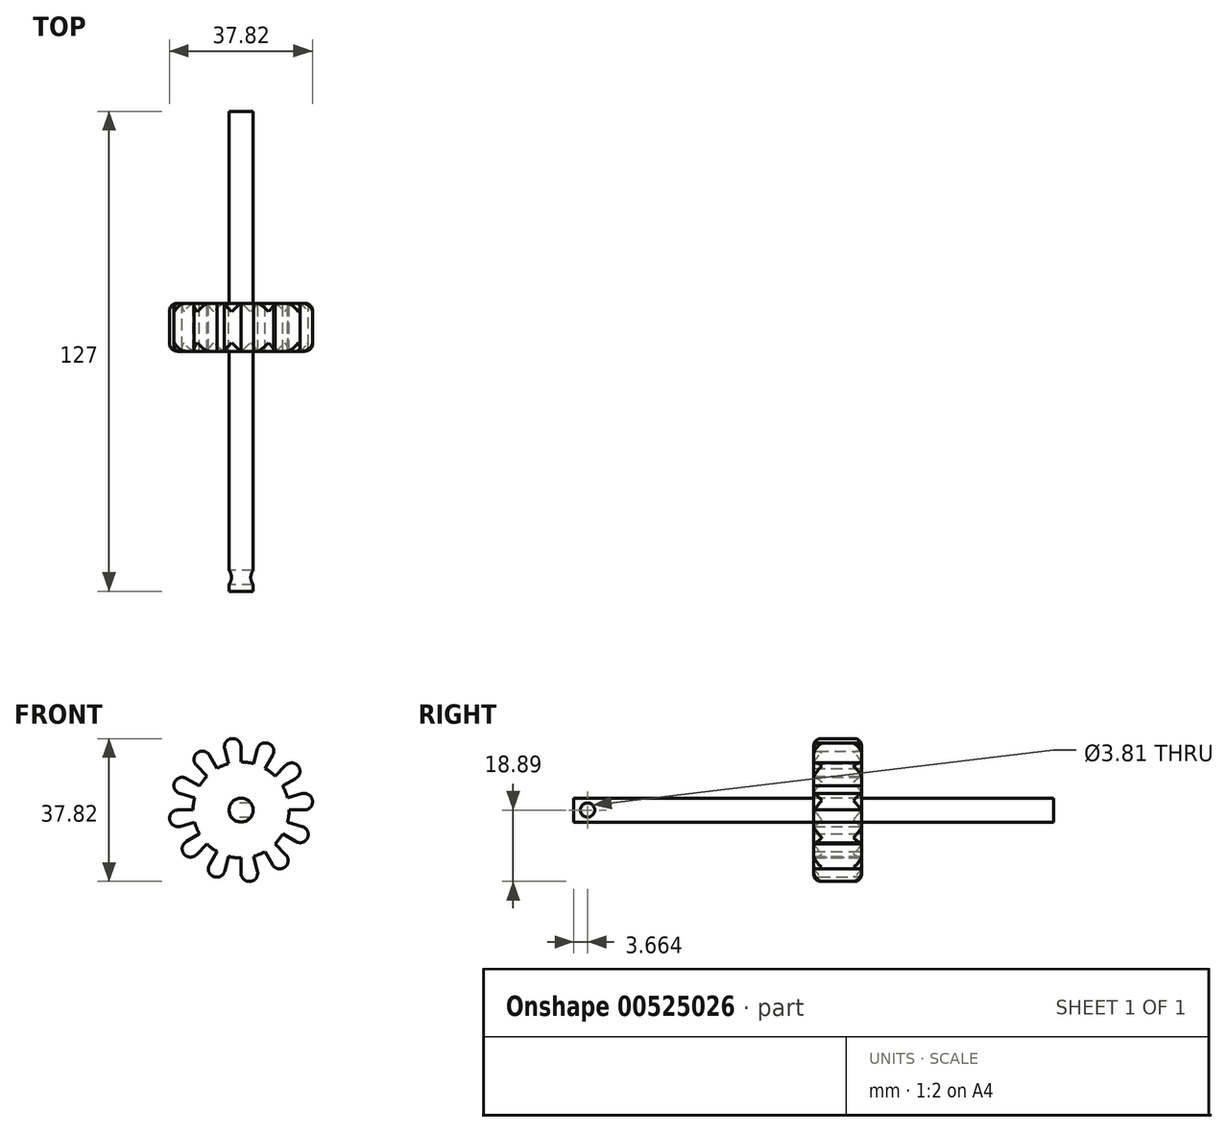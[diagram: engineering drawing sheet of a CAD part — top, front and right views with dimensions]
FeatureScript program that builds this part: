
annotation { "Feature Type Name" : "Feature", "Feature Type Description" : "" }
export const myFeature = defineFeature(function(context is Context, id is Id, definition is map)
    precondition{}
    {
        {
            var Q0;
            Q0=qCreatedBy(makeId("Front.planeOp"),FACE);
            var sketch = newSketch(context, id + "F0", { "sketchPlane" : qUnion([Q0])});
            skCircle(sketch, "E0", {"center": v(-0.02, 0.02) * mm, "radius": 12.7 * mm});
            skCircle(sketch, "E1", {"center": v(-0.02, 0.02) * mm, "radius": 19.05 * mm});
            skLineSegment(sketch, "E2", {"start": v(-0.02, 0.02) * mm, "end": v(-0.02, 19.07) * mm});
            skLineSegment(sketch, "E3", {"start": v(-0.02, 0.02) * mm, "end": v(4.91, 18.42) * mm});
            skLineSegment(sketch, "E4", {"start": v(-0.02, 0.02) * mm, "end": v(9.5, 16.52) * mm});
            skLineSegment(sketch, "E5", {"start": v(-0.02, 0.02) * mm, "end": v(13.45, 13.5) * mm});
            skLineSegment(sketch, "E6", {"start": v(-0.02, 0.02) * mm, "end": v(16.48, 9.55) * mm});
            skLineSegment(sketch, "E7", {"start": v(-0.02, 0.02) * mm, "end": v(18.38, 4.95) * mm});
            skLineSegment(sketch, "E8", {"start": v(-0.02, 0.02) * mm, "end": v(19.03, 0.02) * mm});
            skLineSegment(sketch, "E9", {"start": v(-0.02, 0.02) * mm, "end": v(18.38, -4.9) * mm});
            skLineSegment(sketch, "E10", {"start": v(-0.02, 0.02) * mm, "end": v(16.48, -9.5) * mm});
            skLineSegment(sketch, "E11", {"start": v(-0.02, 0.02) * mm, "end": v(13.45, -13.45) * mm});
            skLineSegment(sketch, "E12", {"start": v(-0.02, 0.02) * mm, "end": v(9.5, -16.48) * mm});
            skLineSegment(sketch, "E13", {"start": v(-0.02, 0.02) * mm, "end": v(4.91, -18.38) * mm});
            skLineSegment(sketch, "E14", {"start": v(-0.02, 0.02) * mm, "end": v(-0.02, -19.03) * mm});
            skLineSegment(sketch, "E15", {"start": v(-0.02, 0.02) * mm, "end": v(-4.95, -18.38) * mm});
            skLineSegment(sketch, "E16", {"start": v(-0.02, 0.02) * mm, "end": v(-9.54, -16.48) * mm});
            skLineSegment(sketch, "E17", {"start": v(-0.02, 0.02) * mm, "end": v(-13.49, -13.45) * mm});
            skLineSegment(sketch, "E18", {"start": v(-0.02, 0.02) * mm, "end": v(-16.51, -9.5) * mm});
            skLineSegment(sketch, "E19", {"start": v(-0.02, 0.02) * mm, "end": v(-18.42, -4.9) * mm});
            skLineSegment(sketch, "E20", {"start": v(-0.02, 0.02) * mm, "end": v(-19.07, 0.02) * mm});
            skLineSegment(sketch, "E21", {"start": v(-0.02, 0.02) * mm, "end": v(-13.49, 13.5) * mm});
            skLineSegment(sketch, "E22", {"start": v(-0.02, 0.02) * mm, "end": v(-16.51, 9.55) * mm});
            skLineSegment(sketch, "E23", {"start": v(-0.02, 0.02) * mm, "end": v(-18.42, 4.95) * mm});
            skLineSegment(sketch, "E24", {"start": v(-0.02, 0.02) * mm, "end": v(-4.95, 18.42) * mm});
            skLineSegment(sketch, "E25", {"start": v(-0.02, 0.02) * mm, "end": v(-9.54, 16.52) * mm});
            skSolve(sketch);
        }
        {
            var Q0;
            {var subQ0=sQuery(id+"F0.wireOp",EDGE,"E13");var subQ1=sQuery(id+"F0.wireOp",EDGE,"E0");var subQ2=makeQuery(id+"F0.imprint","INTERSECT",VERTEX,{"derivedFrom":[subQ1,subQ0]});Q0=makeQuery(id+"F0.imprint","IMPRINT",FACE,{"disambiguationData":[TD([[makeQuery(id+"F0.imprint","IMPRINT",EDGE,{"disambiguationData":[TD([[subQ2,-1.0]])],"derivedFrom":subQ1}),1.0]])]});}
            var Q1;
            {var subQ0=sQuery(id+"F0.wireOp",EDGE,"E15");var subQ1=sQuery(id+"F0.wireOp",EDGE,"E0");var subQ2=makeQuery(id+"F0.imprint","INTERSECT",VERTEX,{"derivedFrom":[subQ1,subQ0]});Q1=makeQuery(id+"F0.imprint","IMPRINT",FACE,{"disambiguationData":[TD([[makeQuery(id+"F0.imprint","IMPRINT",EDGE,{"disambiguationData":[TD([[subQ2,-1.0]])],"derivedFrom":subQ1}),1.0]])]});}
            var Q2;
            {var subQ0=sQuery(id+"F0.wireOp",EDGE,"E17");var subQ1=sQuery(id+"F0.wireOp",EDGE,"E0");var subQ2=makeQuery(id+"F0.imprint","INTERSECT",VERTEX,{"derivedFrom":[subQ1,subQ0]});Q2=makeQuery(id+"F0.imprint","IMPRINT",FACE,{"disambiguationData":[TD([[makeQuery(id+"F0.imprint","IMPRINT",EDGE,{"disambiguationData":[TD([[subQ2,-1.0]])],"derivedFrom":subQ1}),1.0]])]});}
            var Q3;
            {var subQ0=sQuery(id+"F0.wireOp",EDGE,"E19");var subQ1=sQuery(id+"F0.wireOp",EDGE,"E0");var subQ2=makeQuery(id+"F0.imprint","INTERSECT",VERTEX,{"derivedFrom":[subQ1,subQ0]});Q3=makeQuery(id+"F0.imprint","IMPRINT",FACE,{"disambiguationData":[TD([[makeQuery(id+"F0.imprint","IMPRINT",EDGE,{"disambiguationData":[TD([[subQ2,-1.0]])],"derivedFrom":subQ1}),1.0]])]});}
            var Q4;
            {var subQ0=sQuery(id+"F0.wireOp",EDGE,"E18");var subQ1=sQuery(id+"F0.wireOp",EDGE,"E0");var subQ2=makeQuery(id+"F0.imprint","INTERSECT",VERTEX,{"derivedFrom":[subQ1,subQ0]});Q4=makeQuery(id+"F0.imprint","IMPRINT",FACE,{"disambiguationData":[TD([[makeQuery(id+"F0.imprint","IMPRINT",EDGE,{"disambiguationData":[TD([[subQ2,-1.0]])],"derivedFrom":subQ1}),1.0]])]});}
            var Q5;
            {var subQ0=sQuery(id+"F0.wireOp",EDGE,"E16");var subQ1=sQuery(id+"F0.wireOp",EDGE,"E0");var subQ2=makeQuery(id+"F0.imprint","INTERSECT",VERTEX,{"derivedFrom":[subQ1,subQ0]});Q5=makeQuery(id+"F0.imprint","IMPRINT",FACE,{"disambiguationData":[TD([[makeQuery(id+"F0.imprint","IMPRINT",EDGE,{"disambiguationData":[TD([[subQ2,-1.0]])],"derivedFrom":subQ1}),1.0]])]});}
            var Q6;
            {var subQ0=sQuery(id+"F0.wireOp",EDGE,"E14");var subQ1=sQuery(id+"F0.wireOp",EDGE,"E0");var subQ2=makeQuery(id+"F0.imprint","INTERSECT",VERTEX,{"derivedFrom":[subQ1,subQ0]});Q6=makeQuery(id+"F0.imprint","IMPRINT",FACE,{"disambiguationData":[TD([[makeQuery(id+"F0.imprint","IMPRINT",EDGE,{"disambiguationData":[TD([[subQ2,-1.0]])],"derivedFrom":subQ1}),1.0]])]});}
            var Q7;
            {var subQ0=sQuery(id+"F0.wireOp",EDGE,"E12");var subQ1=sQuery(id+"F0.wireOp",EDGE,"E0");var subQ2=makeQuery(id+"F0.imprint","INTERSECT",VERTEX,{"derivedFrom":[subQ1,subQ0]});Q7=makeQuery(id+"F0.imprint","IMPRINT",FACE,{"disambiguationData":[TD([[makeQuery(id+"F0.imprint","IMPRINT",EDGE,{"disambiguationData":[TD([[subQ2,-1.0]])],"derivedFrom":subQ1}),1.0]])]});}
            var Q8;
            {var subQ0=sQuery(id+"F0.wireOp",EDGE,"E11");var subQ1=sQuery(id+"F0.wireOp",EDGE,"E0");var subQ2=makeQuery(id+"F0.imprint","INTERSECT",VERTEX,{"derivedFrom":[subQ1,subQ0]});Q8=makeQuery(id+"F0.imprint","IMPRINT",FACE,{"disambiguationData":[TD([[makeQuery(id+"F0.imprint","IMPRINT",EDGE,{"disambiguationData":[TD([[subQ2,-1.0]])],"derivedFrom":subQ1}),1.0]])]});}
            var Q9;
            {var subQ0=sQuery(id+"F0.wireOp",EDGE,"E10");var subQ1=sQuery(id+"F0.wireOp",EDGE,"E0");var subQ2=makeQuery(id+"F0.imprint","INTERSECT",VERTEX,{"derivedFrom":[subQ1,subQ0]});Q9=makeQuery(id+"F0.imprint","IMPRINT",FACE,{"disambiguationData":[TD([[makeQuery(id+"F0.imprint","IMPRINT",EDGE,{"disambiguationData":[TD([[subQ2,-1.0]])],"derivedFrom":subQ1}),1.0]])]});}
            var Q10;
            {var subQ0=sQuery(id+"F0.wireOp",EDGE,"E8");var subQ1=sQuery(id+"F0.wireOp",EDGE,"E0");var subQ2=makeQuery(id+"F0.imprint","INTERSECT",VERTEX,{"derivedFrom":[subQ1,subQ0]});Q10=makeQuery(id+"F0.imprint","IMPRINT",FACE,{"disambiguationData":[TD([[makeQuery(id+"F0.imprint","IMPRINT",EDGE,{"disambiguationData":[TD([[subQ2,1.0]])],"derivedFrom":subQ1}),1.0]])]});}
            var Q11;
            {var subQ0=sQuery(id+"F0.wireOp",EDGE,"E7");var subQ1=sQuery(id+"F0.wireOp",EDGE,"E0");var subQ2=makeQuery(id+"F0.imprint","INTERSECT",VERTEX,{"derivedFrom":[subQ1,subQ0]});Q11=makeQuery(id+"F0.imprint","IMPRINT",FACE,{"disambiguationData":[TD([[makeQuery(id+"F0.imprint","IMPRINT",EDGE,{"disambiguationData":[TD([[subQ2,1.0]])],"derivedFrom":subQ1}),1.0]])]});}
            var Q12;
            {var subQ0=sQuery(id+"F0.wireOp",EDGE,"E7");var subQ1=sQuery(id+"F0.wireOp",EDGE,"E0");var subQ2=makeQuery(id+"F0.imprint","INTERSECT",VERTEX,{"derivedFrom":[subQ1,subQ0]});Q12=makeQuery(id+"F0.imprint","IMPRINT",FACE,{"disambiguationData":[TD([[makeQuery(id+"F0.imprint","IMPRINT",EDGE,{"disambiguationData":[TD([[subQ2,-1.0]])],"derivedFrom":subQ1}),1.0]])]});}
            var Q13;
            {var subQ0=sQuery(id+"F0.wireOp",EDGE,"E6");var subQ1=sQuery(id+"F0.wireOp",EDGE,"E0");var subQ2=makeQuery(id+"F0.imprint","INTERSECT",VERTEX,{"derivedFrom":[subQ1,subQ0]});Q13=makeQuery(id+"F0.imprint","IMPRINT",FACE,{"disambiguationData":[TD([[makeQuery(id+"F0.imprint","IMPRINT",EDGE,{"disambiguationData":[TD([[subQ2,-1.0]])],"derivedFrom":subQ1}),1.0]])]});}
            var Q14;
            {var subQ0=sQuery(id+"F0.wireOp",EDGE,"E5");var subQ1=sQuery(id+"F0.wireOp",EDGE,"E0");var subQ2=makeQuery(id+"F0.imprint","INTERSECT",VERTEX,{"derivedFrom":[subQ1,subQ0]});Q14=makeQuery(id+"F0.imprint","IMPRINT",FACE,{"disambiguationData":[TD([[makeQuery(id+"F0.imprint","IMPRINT",EDGE,{"disambiguationData":[TD([[subQ2,-1.0]])],"derivedFrom":subQ1}),1.0]])]});}
            var Q15;
            {var subQ0=sQuery(id+"F0.wireOp",EDGE,"E4");var subQ1=sQuery(id+"F0.wireOp",EDGE,"E0");var subQ2=makeQuery(id+"F0.imprint","INTERSECT",VERTEX,{"derivedFrom":[subQ1,subQ0]});Q15=makeQuery(id+"F0.imprint","IMPRINT",FACE,{"disambiguationData":[TD([[makeQuery(id+"F0.imprint","IMPRINT",EDGE,{"disambiguationData":[TD([[subQ2,-1.0]])],"derivedFrom":subQ1}),1.0]])]});}
            var Q16;
            {var subQ0=sQuery(id+"F0.wireOp",EDGE,"E3");var subQ1=sQuery(id+"F0.wireOp",EDGE,"E0");var subQ2=makeQuery(id+"F0.imprint","INTERSECT",VERTEX,{"derivedFrom":[subQ1,subQ0]});Q16=makeQuery(id+"F0.imprint","IMPRINT",FACE,{"disambiguationData":[TD([[makeQuery(id+"F0.imprint","IMPRINT",EDGE,{"disambiguationData":[TD([[subQ2,-1.0]])],"derivedFrom":subQ1}),1.0]])]});}
            var Q17;
            {var subQ0=sQuery(id+"F0.wireOp",EDGE,"E2");var subQ1=sQuery(id+"F0.wireOp",EDGE,"E0");var subQ2=makeQuery(id+"F0.imprint","INTERSECT",VERTEX,{"derivedFrom":[subQ1,subQ0]});Q17=makeQuery(id+"F0.imprint","IMPRINT",FACE,{"disambiguationData":[TD([[makeQuery(id+"F0.imprint","IMPRINT",EDGE,{"disambiguationData":[TD([[subQ2,-1.0]])],"derivedFrom":subQ1}),1.0]])]});}
            var Q18;
            {var subQ0=sQuery(id+"F0.wireOp",EDGE,"E24");var subQ1=sQuery(id+"F0.wireOp",EDGE,"E0");var subQ2=makeQuery(id+"F0.imprint","INTERSECT",VERTEX,{"derivedFrom":[subQ1,subQ0]});Q18=makeQuery(id+"F0.imprint","IMPRINT",FACE,{"disambiguationData":[TD([[makeQuery(id+"F0.imprint","IMPRINT",EDGE,{"disambiguationData":[TD([[subQ2,-1.0]])],"derivedFrom":subQ1}),1.0]])]});}
            var Q19;
            {var subQ0=sQuery(id+"F0.wireOp",EDGE,"E25");var subQ1=sQuery(id+"F0.wireOp",EDGE,"E0");var subQ2=makeQuery(id+"F0.imprint","INTERSECT",VERTEX,{"derivedFrom":[subQ1,subQ0]});Q19=makeQuery(id+"F0.imprint","IMPRINT",FACE,{"disambiguationData":[TD([[makeQuery(id+"F0.imprint","IMPRINT",EDGE,{"disambiguationData":[TD([[subQ2,-1.0]])],"derivedFrom":subQ1}),1.0]])]});}
            var Q20;
            {var subQ0=sQuery(id+"F0.wireOp",EDGE,"E21");var subQ1=sQuery(id+"F0.wireOp",EDGE,"E0");var subQ2=makeQuery(id+"F0.imprint","INTERSECT",VERTEX,{"derivedFrom":[subQ1,subQ0]});Q20=makeQuery(id+"F0.imprint","IMPRINT",FACE,{"disambiguationData":[TD([[makeQuery(id+"F0.imprint","IMPRINT",EDGE,{"disambiguationData":[TD([[subQ2,-1.0]])],"derivedFrom":subQ1}),1.0]])]});}
            var Q21;
            {var subQ0=sQuery(id+"F0.wireOp",EDGE,"E22");var subQ1=sQuery(id+"F0.wireOp",EDGE,"E0");var subQ2=makeQuery(id+"F0.imprint","INTERSECT",VERTEX,{"derivedFrom":[subQ1,subQ0]});Q21=makeQuery(id+"F0.imprint","IMPRINT",FACE,{"disambiguationData":[TD([[makeQuery(id+"F0.imprint","IMPRINT",EDGE,{"disambiguationData":[TD([[subQ2,-1.0]])],"derivedFrom":subQ1}),1.0]])]});}
            var Q22;
            {var subQ0=sQuery(id+"F0.wireOp",EDGE,"E23");var subQ1=sQuery(id+"F0.wireOp",EDGE,"E0");var subQ2=makeQuery(id+"F0.imprint","INTERSECT",VERTEX,{"derivedFrom":[subQ1,subQ0]});Q22=makeQuery(id+"F0.imprint","IMPRINT",FACE,{"disambiguationData":[TD([[makeQuery(id+"F0.imprint","IMPRINT",EDGE,{"disambiguationData":[TD([[subQ2,-1.0]])],"derivedFrom":subQ1}),1.0]])]});}
            var Q23;
            {var subQ0=sQuery(id+"F0.wireOp",EDGE,"E20");var subQ1=sQuery(id+"F0.wireOp",EDGE,"E0");var subQ2=makeQuery(id+"F0.imprint","INTERSECT",VERTEX,{"derivedFrom":[subQ1,subQ0]});Q23=makeQuery(id+"F0.imprint","IMPRINT",FACE,{"disambiguationData":[TD([[makeQuery(id+"F0.imprint","IMPRINT",EDGE,{"disambiguationData":[TD([[subQ2,-1.0]])],"derivedFrom":subQ1}),1.0]])]});}
            var Q24;
            {var subQ0=sQuery(id+"F0.wireOp",EDGE,"E22");var subQ1=sQuery(id+"F0.wireOp",EDGE,"E0");var subQ2=makeQuery(id+"F0.imprint","INTERSECT",VERTEX,{"derivedFrom":[subQ1,subQ0]});Q24=makeQuery(id+"F0.imprint","IMPRINT",FACE,{"disambiguationData":[TD([[makeQuery(id+"F0.imprint","IMPRINT",EDGE,{"disambiguationData":[TD([[subQ2,-1.0]])],"derivedFrom":subQ1}),-1.0]])]});}
            var Q25;
            {var subQ0=sQuery(id+"F0.wireOp",EDGE,"E20");var subQ1=sQuery(id+"F0.wireOp",EDGE,"E0");var subQ2=makeQuery(id+"F0.imprint","INTERSECT",VERTEX,{"derivedFrom":[subQ1,subQ0]});Q25=makeQuery(id+"F0.imprint","IMPRINT",FACE,{"disambiguationData":[TD([[makeQuery(id+"F0.imprint","IMPRINT",EDGE,{"disambiguationData":[TD([[subQ2,-1.0]])],"derivedFrom":subQ1}),-1.0]])]});}
            var Q26;
            {var subQ0=sQuery(id+"F0.wireOp",EDGE,"E18");var subQ1=sQuery(id+"F0.wireOp",EDGE,"E0");var subQ2=makeQuery(id+"F0.imprint","INTERSECT",VERTEX,{"derivedFrom":[subQ1,subQ0]});Q26=makeQuery(id+"F0.imprint","IMPRINT",FACE,{"disambiguationData":[TD([[makeQuery(id+"F0.imprint","IMPRINT",EDGE,{"disambiguationData":[TD([[subQ2,-1.0]])],"derivedFrom":subQ1}),-1.0]])]});}
            var Q27;
            {var subQ0=sQuery(id+"F0.wireOp",EDGE,"E16");var subQ1=sQuery(id+"F0.wireOp",EDGE,"E0");var subQ2=makeQuery(id+"F0.imprint","INTERSECT",VERTEX,{"derivedFrom":[subQ1,subQ0]});Q27=makeQuery(id+"F0.imprint","IMPRINT",FACE,{"disambiguationData":[TD([[makeQuery(id+"F0.imprint","IMPRINT",EDGE,{"disambiguationData":[TD([[subQ2,-1.0]])],"derivedFrom":subQ1}),-1.0]])]});}
            var Q28;
            {var subQ0=sQuery(id+"F0.wireOp",EDGE,"E10");var subQ1=sQuery(id+"F0.wireOp",EDGE,"E0");var subQ2=makeQuery(id+"F0.imprint","INTERSECT",VERTEX,{"derivedFrom":[subQ1,subQ0]});Q28=makeQuery(id+"F0.imprint","IMPRINT",FACE,{"disambiguationData":[TD([[makeQuery(id+"F0.imprint","IMPRINT",EDGE,{"disambiguationData":[TD([[subQ2,-1.0]])],"derivedFrom":subQ1}),-1.0]])]});}
            var Q29;
            {var subQ0=sQuery(id+"F0.wireOp",EDGE,"E7");var subQ1=sQuery(id+"F0.wireOp",EDGE,"E0");var subQ2=makeQuery(id+"F0.imprint","INTERSECT",VERTEX,{"derivedFrom":[subQ1,subQ0]});Q29=makeQuery(id+"F0.imprint","IMPRINT",FACE,{"disambiguationData":[TD([[makeQuery(id+"F0.imprint","IMPRINT",EDGE,{"disambiguationData":[TD([[subQ2,1.0]])],"derivedFrom":subQ1}),-1.0]])]});}
            var Q30;
            {var subQ0=sQuery(id+"F0.wireOp",EDGE,"E6");var subQ1=sQuery(id+"F0.wireOp",EDGE,"E0");var subQ2=makeQuery(id+"F0.imprint","INTERSECT",VERTEX,{"derivedFrom":[subQ1,subQ0]});Q30=makeQuery(id+"F0.imprint","IMPRINT",FACE,{"disambiguationData":[TD([[makeQuery(id+"F0.imprint","IMPRINT",EDGE,{"disambiguationData":[TD([[subQ2,-1.0]])],"derivedFrom":subQ1}),-1.0]])]});}
            var Q31;
            {var subQ0=sQuery(id+"F0.wireOp",EDGE,"E4");var subQ1=sQuery(id+"F0.wireOp",EDGE,"E0");var subQ2=makeQuery(id+"F0.imprint","INTERSECT",VERTEX,{"derivedFrom":[subQ1,subQ0]});Q31=makeQuery(id+"F0.imprint","IMPRINT",FACE,{"disambiguationData":[TD([[makeQuery(id+"F0.imprint","IMPRINT",EDGE,{"disambiguationData":[TD([[subQ2,-1.0]])],"derivedFrom":subQ1}),-1.0]])]});}
            var Q32;
            {var subQ0=sQuery(id+"F0.wireOp",EDGE,"E2");var subQ1=sQuery(id+"F0.wireOp",EDGE,"E0");var subQ2=makeQuery(id+"F0.imprint","INTERSECT",VERTEX,{"derivedFrom":[subQ1,subQ0]});Q32=makeQuery(id+"F0.imprint","IMPRINT",FACE,{"disambiguationData":[TD([[makeQuery(id+"F0.imprint","IMPRINT",EDGE,{"disambiguationData":[TD([[subQ2,-1.0]])],"derivedFrom":subQ1}),-1.0]])]});}
            var Q33;
            {var subQ0=sQuery(id+"F0.wireOp",EDGE,"E25");var subQ1=sQuery(id+"F0.wireOp",EDGE,"E0");var subQ2=makeQuery(id+"F0.imprint","INTERSECT",VERTEX,{"derivedFrom":[subQ1,subQ0]});Q33=makeQuery(id+"F0.imprint","IMPRINT",FACE,{"disambiguationData":[TD([[makeQuery(id+"F0.imprint","IMPRINT",EDGE,{"disambiguationData":[TD([[subQ2,-1.0]])],"derivedFrom":subQ1}),-1.0]])]});}
            var Q34;
            {var subQ0=sQuery(id+"F0.wireOp",EDGE,"E14");var subQ1=sQuery(id+"F0.wireOp",EDGE,"E0");var subQ2=makeQuery(id+"F0.imprint","INTERSECT",VERTEX,{"derivedFrom":[subQ1,subQ0]});Q34=makeQuery(id+"F0.imprint","IMPRINT",FACE,{"disambiguationData":[TD([[makeQuery(id+"F0.imprint","IMPRINT",EDGE,{"disambiguationData":[TD([[subQ2,-1.0]])],"derivedFrom":subQ1}),-1.0]])]});}
            var Q35;
            {var subQ0=sQuery(id+"F0.wireOp",EDGE,"E12");var subQ1=sQuery(id+"F0.wireOp",EDGE,"E0");var subQ2=makeQuery(id+"F0.imprint","INTERSECT",VERTEX,{"derivedFrom":[subQ1,subQ0]});Q35=makeQuery(id+"F0.imprint","IMPRINT",FACE,{"disambiguationData":[TD([[makeQuery(id+"F0.imprint","IMPRINT",EDGE,{"disambiguationData":[TD([[subQ2,-1.0]])],"derivedFrom":subQ1}),-1.0]])]});}
            extrude(context, id + "F1", {"entities" : qUnion([Q0, Q1, Q2, Q3, Q4, Q5, Q6, Q7, Q8, Q9, Q10, Q11, Q12, Q13, Q14, Q15, Q16, Q17, Q18, Q19, Q20, Q21, Q22, Q23, Q24, Q25, Q26, Q27, Q28, Q29, Q30, Q31, Q32, Q33, Q34, Q35]), "depth" : 12.7 * mm, "offsetDistance" : 25.4 * mm});
        }
        {
            var Q0;
            {var subQ0=sQuery(id+"F0.wireOp",EDGE,"E1");Q0=makeQuery(id+"F1.opExtrude","SWEPT_FACE",FACE,{"disambiguationData":[OSD([subQ0]),TDD([makeQuery(id+"F0.imprint","IMPRINT",EDGE,{"disambiguationData":[TD([[makeQuery(id+"F0.imprint","INTERSECT",VERTEX,{"derivedFrom":[subQ0,sQuery(id+"F0.wireOp",EDGE,"E11")]}),1.0]])],"derivedFrom":subQ0})])]});}
            var Q1;
            {var subQ0=sQuery(id+"F0.wireOp",EDGE,"E1");Q1=makeQuery(id+"F1.opExtrude","SWEPT_FACE",FACE,{"disambiguationData":[OSD([subQ0]),TDD([makeQuery(id+"F0.imprint","IMPRINT",EDGE,{"disambiguationData":[TD([[makeQuery(id+"F0.imprint","INTERSECT",VERTEX,{"derivedFrom":[subQ0,sQuery(id+"F0.wireOp",EDGE,"E9")]}),1.0]])],"derivedFrom":subQ0})])]});}
            var Q2;
            {var subQ0=sQuery(id+"F0.wireOp",EDGE,"E1");Q2=makeQuery(id+"F1.opExtrude","SWEPT_FACE",FACE,{"disambiguationData":[OSD([subQ0]),TDD([makeQuery(id+"F0.imprint","IMPRINT",EDGE,{"disambiguationData":[TD([[makeQuery(id+"F0.imprint","INTERSECT",VERTEX,{"derivedFrom":[subQ0,sQuery(id+"F0.wireOp",EDGE,"E13")]}),1.0]])],"derivedFrom":subQ0})])]});}
            var Q3;
            {var subQ0=sQuery(id+"F0.wireOp",EDGE,"E1");Q3=makeQuery(id+"F1.opExtrude","SWEPT_FACE",FACE,{"disambiguationData":[OSD([subQ0]),TDD([makeQuery(id+"F0.imprint","IMPRINT",EDGE,{"disambiguationData":[TD([[makeQuery(id+"F0.imprint","INTERSECT",VERTEX,{"derivedFrom":[subQ0,sQuery(id+"F0.wireOp",EDGE,"E7")]}),1.0]])],"derivedFrom":subQ0})])]});}
            var Q4;
            {var subQ0=sQuery(id+"F0.wireOp",EDGE,"E1");Q4=makeQuery(id+"F1.opExtrude","SWEPT_FACE",FACE,{"disambiguationData":[OSD([subQ0]),TDD([makeQuery(id+"F0.imprint","IMPRINT",EDGE,{"disambiguationData":[TD([[makeQuery(id+"F0.imprint","INTERSECT",VERTEX,{"derivedFrom":[subQ0,sQuery(id+"F0.wireOp",EDGE,"E5")]}),1.0]])],"derivedFrom":subQ0})])]});}
            var Q5;
            {var subQ0=sQuery(id+"F0.wireOp",EDGE,"E1");Q5=makeQuery(id+"F1.opExtrude","SWEPT_FACE",FACE,{"disambiguationData":[OSD([subQ0]),TDD([makeQuery(id+"F0.imprint","IMPRINT",EDGE,{"disambiguationData":[TD([[makeQuery(id+"F0.imprint","INTERSECT",VERTEX,{"derivedFrom":[subQ0,sQuery(id+"F0.wireOp",EDGE,"E3")]}),1.0]])],"derivedFrom":subQ0})])]});}
            var Q6;
            {var subQ0=sQuery(id+"F0.wireOp",EDGE,"E1");Q6=makeQuery(id+"F1.opExtrude","SWEPT_FACE",FACE,{"disambiguationData":[OSD([subQ0]),TDD([makeQuery(id+"F0.imprint","IMPRINT",EDGE,{"disambiguationData":[TD([[makeQuery(id+"F0.imprint","INTERSECT",VERTEX,{"derivedFrom":[subQ0,sQuery(id+"F0.wireOp",EDGE,"E2")]}),-1.0]])],"derivedFrom":subQ0})])]});}
            var Q7;
            {var subQ0=sQuery(id+"F0.wireOp",EDGE,"E1");Q7=makeQuery(id+"F1.opExtrude","SWEPT_FACE",FACE,{"disambiguationData":[OSD([subQ0]),TDD([makeQuery(id+"F0.imprint","IMPRINT",EDGE,{"disambiguationData":[TD([[makeQuery(id+"F0.imprint","INTERSECT",VERTEX,{"derivedFrom":[subQ0,sQuery(id+"F0.wireOp",EDGE,"E21")]}),1.0]])],"derivedFrom":subQ0})])]});}
            var Q8;
            {var subQ0=sQuery(id+"F0.wireOp",EDGE,"E1");Q8=makeQuery(id+"F1.opExtrude","SWEPT_FACE",FACE,{"disambiguationData":[OSD([subQ0]),TDD([makeQuery(id+"F0.imprint","IMPRINT",EDGE,{"disambiguationData":[TD([[makeQuery(id+"F0.imprint","INTERSECT",VERTEX,{"derivedFrom":[subQ0,sQuery(id+"F0.wireOp",EDGE,"E22")]}),-1.0]])],"derivedFrom":subQ0})])]});}
            var Q9;
            {var subQ0=sQuery(id+"F0.wireOp",EDGE,"E1");Q9=makeQuery(id+"F1.opExtrude","SWEPT_FACE",FACE,{"disambiguationData":[OSD([subQ0]),TDD([makeQuery(id+"F0.imprint","IMPRINT",EDGE,{"disambiguationData":[TD([[makeQuery(id+"F0.imprint","INTERSECT",VERTEX,{"derivedFrom":[subQ0,sQuery(id+"F0.wireOp",EDGE,"E19")]}),1.0]])],"derivedFrom":subQ0})])]});}
            var Q10;
            {var subQ0=sQuery(id+"F0.wireOp",EDGE,"E1");Q10=makeQuery(id+"F1.opExtrude","SWEPT_FACE",FACE,{"disambiguationData":[OSD([subQ0]),TDD([makeQuery(id+"F0.imprint","IMPRINT",EDGE,{"disambiguationData":[TD([[makeQuery(id+"F0.imprint","INTERSECT",VERTEX,{"derivedFrom":[subQ0,sQuery(id+"F0.wireOp",EDGE,"E17")]}),1.0]])],"derivedFrom":subQ0})])]});}
            var Q11;
            {var subQ0=sQuery(id+"F0.wireOp",EDGE,"E1");Q11=makeQuery(id+"F1.opExtrude","SWEPT_FACE",FACE,{"disambiguationData":[OSD([subQ0]),TDD([makeQuery(id+"F0.imprint","IMPRINT",EDGE,{"disambiguationData":[TD([[makeQuery(id+"F0.imprint","INTERSECT",VERTEX,{"derivedFrom":[subQ0,sQuery(id+"F0.wireOp",EDGE,"E15")]}),1.0]])],"derivedFrom":subQ0})])]});}
            fillet(context, id + "F2", {"entities" : qUnion([Q0, Q1, Q2, Q3, Q4, Q5, Q6, Q7, Q8, Q9, Q10, Q11]), "radius" : 2.18 * mm, "tangentPropagation" : true, "allowEdgeOverflow" : false});
        }
        {
            var Q0;
            Q0=makeQuery(id+"F1.opExtrude","CAP_FACE",FACE,{"disambiguationData":[OSD([sQuery(id+"F0.wireOp",EDGE,"E0"),sQuery(id+"F0.wireOp",EDGE,"E1"),sQuery(id+"F0.wireOp",EDGE,"E2"),sQuery(id+"F0.wireOp",EDGE,"E3"),sQuery(id+"F0.wireOp",EDGE,"E4"),sQuery(id+"F0.wireOp",EDGE,"E5"),sQuery(id+"F0.wireOp",EDGE,"E6"),sQuery(id+"F0.wireOp",EDGE,"E7"),sQuery(id+"F0.wireOp",EDGE,"E8"),sQuery(id+"F0.wireOp",EDGE,"E9"),sQuery(id+"F0.wireOp",EDGE,"E10"),sQuery(id+"F0.wireOp",EDGE,"E11"),sQuery(id+"F0.wireOp",EDGE,"E12"),sQuery(id+"F0.wireOp",EDGE,"E13"),sQuery(id+"F0.wireOp",EDGE,"E14"),sQuery(id+"F0.wireOp",EDGE,"E15"),sQuery(id+"F0.wireOp",EDGE,"E16"),sQuery(id+"F0.wireOp",EDGE,"E17"),sQuery(id+"F0.wireOp",EDGE,"E18"),sQuery(id+"F0.wireOp",EDGE,"E19"),sQuery(id+"F0.wireOp",EDGE,"E20"),sQuery(id+"F0.wireOp",EDGE,"E21"),sQuery(id+"F0.wireOp",EDGE,"E22"),sQuery(id+"F0.wireOp",EDGE,"E23"),sQuery(id+"F0.wireOp",EDGE,"E24"),sQuery(id+"F0.wireOp",EDGE,"E25")])],"isStart":false});
            var sketch = newSketch(context, id + "F3", { "sketchPlane" : qUnion([Q0])});
            skCircle(sketch, "E26", {"center": v(0, 0) * mm, "radius": 3.18 * mm});
            skSolve(sketch);
        }
        {
            var Q0;
            Q0=makeQuery(id+"F3.imprint","IMPRINT",FACE,{"disambiguationData":[TD([[makeQuery(id+"F3.imprint","IMPRINT",EDGE,{"derivedFrom":sQuery(id+"F3.wireOp",EDGE,"E26")}),1.0]])]});
            extrude(context, id + "F4", {"entities" : qUnion([Q0]), "operationType" : NewBodyOperationType.ADD, "depth" : 63.5 * mm, "offsetDistance" : 25.4 * mm, "hasSecondDirection" : true, "secondDirectionOppositeDirection" : true, "secondDirectionDepth" : 63.5 * mm});
        }
        {
            var Q0;
            Q0=qCreatedBy(makeId("Right.planeOp"),FACE);
            var sketch = newSketch(context, id + "F5", { "sketchPlane" : qUnion([Q0])});
            skCircle(sketch, "E27", {"center": v(-72.54, 0) * mm, "radius": 1.9 * mm});
            skSolve(sketch);
        }
        {
            var Q0;
            Q0 = qSketchRegion(id + "F5", true);
            extrude(context, id + "F6", {"entities" : qUnion([Q0]), "operationType" : NewBodyOperationType.REMOVE, "depth" : 6.35 * mm, "offsetDistance" : 25.4 * mm, "hasSecondDirection" : true, "secondDirectionOppositeDirection" : true, "secondDirectionDepth" : 6.35 * mm});
        }
    });
